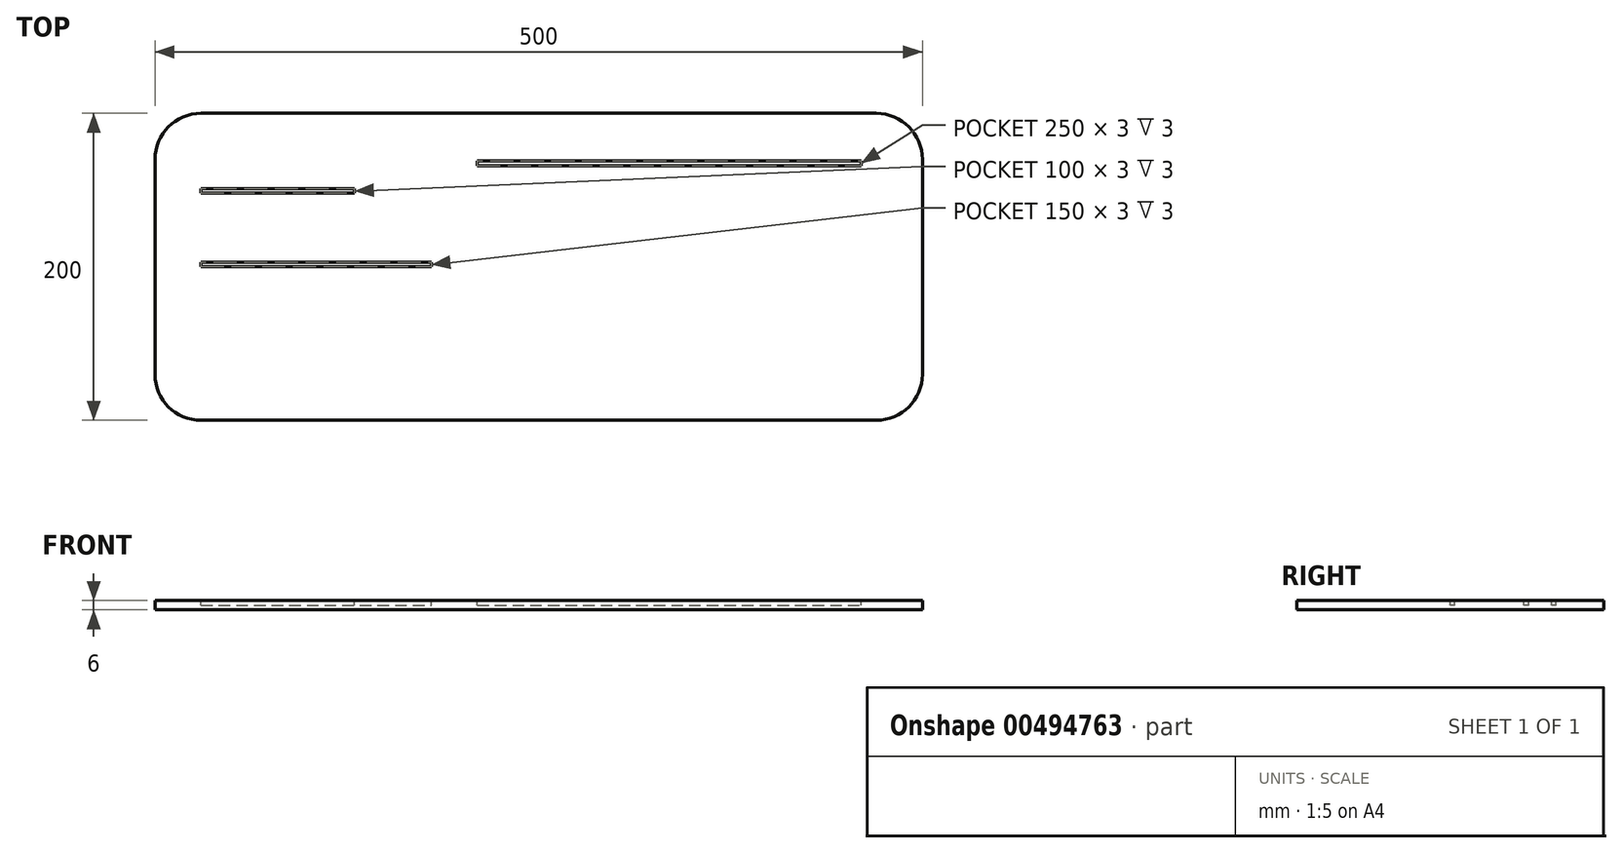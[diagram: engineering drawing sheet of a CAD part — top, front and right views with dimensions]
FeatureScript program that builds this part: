
annotation { "Feature Type Name" : "Feature", "Feature Type Description" : "" }
export const myFeature = defineFeature(function(context is Context, id is Id, definition is map)
    precondition{}
    {
        {
            var Q0;
            Q0=qCreatedBy(makeId("Top.planeOp"),FACE);
            var sketch = newSketch(context, id + "F0", { "sketchPlane" : qUnion([Q0])});
            skLineSegment(sketch, "E0.bottom", {"start": v(250, -100) * mm, "end": v(-250, -100) * mm});
            skLineSegment(sketch, "E0.top", {"start": v(250, 100) * mm, "end": v(-250, 100) * mm});
            skLineSegment(sketch, "E0.left", {"start": v(250, -100) * mm, "end": v(250, 100) * mm});
            skLineSegment(sketch, "E0.right", {"start": v(-250, -100) * mm, "end": v(-250, 100) * mm});
            skPoint(sketch, "E0.middle", {"position": v(0, 0) * mm});
            skSolve(sketch);
        }
        {
            var Q0;
            Q0 = qSketchRegion(id + "F0", true);
            extrude(context, id + "F1", {"entities" : qUnion([Q0]), "depth" : 3 * mm});
        }
        {
            var Q0;
            Q0=makeQuery(id+"F1.opExtrude","SWEPT_EDGE",EDGE,{"disambiguationData":[OSD([sQuery(id+"F0.wireOp",EDGE,"E0.bottom"),sQuery(id+"F0.wireOp",EDGE,"E0.right")])]});
            var Q1;
            Q1=makeQuery(id+"F1.opExtrude","SWEPT_EDGE",EDGE,{"disambiguationData":[OSD([sQuery(id+"F0.wireOp",EDGE,"E0.top"),sQuery(id+"F0.wireOp",EDGE,"E0.left")])]});
            var Q2;
            Q2=makeQuery(id+"F1.opExtrude","SWEPT_EDGE",EDGE,{"disambiguationData":[OSD([sQuery(id+"F0.wireOp",EDGE,"E0.top"),sQuery(id+"F0.wireOp",EDGE,"E0.right")])]});
            var Q3;
            Q3=makeQuery(id+"F1.opExtrude","SWEPT_EDGE",EDGE,{"disambiguationData":[OSD([sQuery(id+"F0.wireOp",EDGE,"E0.bottom"),sQuery(id+"F0.wireOp",EDGE,"E0.left")])]});
            fillet(context, id + "F2", {"entities" : qUnion([Q0, Q1, Q2, Q3]), "radius" : 30 * mm, "tangentPropagation" : true, "allowEdgeOverflow" : false});
        }
        {
            var Q0;
            Q0=makeQuery(id+"F1.opExtrude","CAP_FACE",FACE,{"disambiguationData":[OSD([sQuery(id+"F0.wireOp",EDGE,"E0.bottom"),sQuery(id+"F0.wireOp",EDGE,"E0.top"),sQuery(id+"F0.wireOp",EDGE,"E0.left"),sQuery(id+"F0.wireOp",EDGE,"E0.right")])],"isStart":false});
            var sketch = newSketch(context, id + "F3", { "sketchPlane" : qUnion([Q0])});
            skLineSegment(sketch, "E1.bottom", {"start": v(-220, 51) * mm, "end": v(-120, 51) * mm});
            skLineSegment(sketch, "E1.top", {"start": v(-220, 48) * mm, "end": v(-120, 48) * mm});
            skLineSegment(sketch, "E1.left", {"start": v(-220, 51) * mm, "end": v(-220, 48) * mm});
            skLineSegment(sketch, "E1.right", {"start": v(-120, 51) * mm, "end": v(-120, 48) * mm});
            skLineSegment(sketch, "E2.bottom", {"start": v(-220, 3) * mm, "end": v(-70, 3) * mm});
            skLineSegment(sketch, "E2.top", {"start": v(-220, 0) * mm, "end": v(-70, 0) * mm});
            skLineSegment(sketch, "E2.left", {"start": v(-220, 3) * mm, "end": v(-220, 0) * mm});
            skLineSegment(sketch, "E2.right", {"start": v(-70, 3) * mm, "end": v(-70, 0) * mm});
            skLineSegment(sketch, "E3.bottom", {"start": v(-40, 69) * mm, "end": v(210, 69) * mm});
            skLineSegment(sketch, "E3.top", {"start": v(-40, 66) * mm, "end": v(210, 66) * mm});
            skLineSegment(sketch, "E3.left", {"start": v(-40, 69) * mm, "end": v(-40, 66) * mm});
            skLineSegment(sketch, "E3.right", {"start": v(210, 69) * mm, "end": v(210, 66) * mm});
            skSolve(sketch);
        }
        {
            var Q0;
            Q0 = qSketchRegion(id + "F3", true);
            extrude(context, id + "F4", {"entities" : qUnion([Q0]), "operationType" : NewBodyOperationType.REMOVE, "oppositeDirection" : true, "depth" : 3 * mm});
        }
        {
            var Q0;
            Q0=makeQuery(id+"F1.opExtrude","CAP_FACE",FACE,{"disambiguationData":[OSD([sQuery(id+"F0.wireOp",EDGE,"E0.bottom"),sQuery(id+"F0.wireOp",EDGE,"E0.top"),sQuery(id+"F0.wireOp",EDGE,"E0.left"),sQuery(id+"F0.wireOp",EDGE,"E0.right")])],"isStart":true});
            var sketch = newSketch(context, id + "F5", { "sketchPlane" : qUnion([Q0])});
            skLineSegment(sketch, "E4.bottom", {"start": v(-250, 100) * mm, "end": v(250, 100) * mm});
            skLineSegment(sketch, "E4.top", {"start": v(-250, -100) * mm, "end": v(250, -100) * mm});
            skLineSegment(sketch, "E4.left", {"start": v(-250, 100) * mm, "end": v(-250, -100) * mm});
            skLineSegment(sketch, "E4.right", {"start": v(250, 100) * mm, "end": v(250, -100) * mm});
            skPoint(sketch, "E4.middle", {"position": v(0, 0) * mm});
            skSolve(sketch);
        }
        {
            var Q0;
            Q0 = qSketchRegion(id + "F5", true);
            extrude(context, id + "F6", {"entities" : qUnion([Q0]), "operationType" : NewBodyOperationType.ADD, "depth" : 3 * mm});
        }
        {
            var Q0;
            Q0=makeQuery(id+"F6.opExtrude","SWEPT_EDGE",EDGE,{"disambiguationData":[OSD([sQuery(id+"F5.wireOp",EDGE,"E4.bottom"),sQuery(id+"F5.wireOp",EDGE,"E4.left")])]});
            var Q1;
            Q1=makeQuery(id+"F6.opExtrude","SWEPT_EDGE",EDGE,{"disambiguationData":[OSD([sQuery(id+"F5.wireOp",EDGE,"E4.top"),sQuery(id+"F5.wireOp",EDGE,"E4.left")])]});
            var Q2;
            Q2=makeQuery(id+"F6.opExtrude","SWEPT_EDGE",EDGE,{"disambiguationData":[OSD([sQuery(id+"F5.wireOp",EDGE,"E4.top"),sQuery(id+"F5.wireOp",EDGE,"E4.right")])]});
            var Q3;
            Q3=makeQuery(id+"F6.opExtrude","SWEPT_EDGE",EDGE,{"disambiguationData":[OSD([sQuery(id+"F5.wireOp",EDGE,"E4.bottom"),sQuery(id+"F5.wireOp",EDGE,"E4.right")])]});
            fillet(context, id + "F7", {"entities" : qUnion([Q0, Q1, Q2, Q3]), "radius" : 30 * mm, "tangentPropagation" : true, "allowEdgeOverflow" : false});
        }
    });
